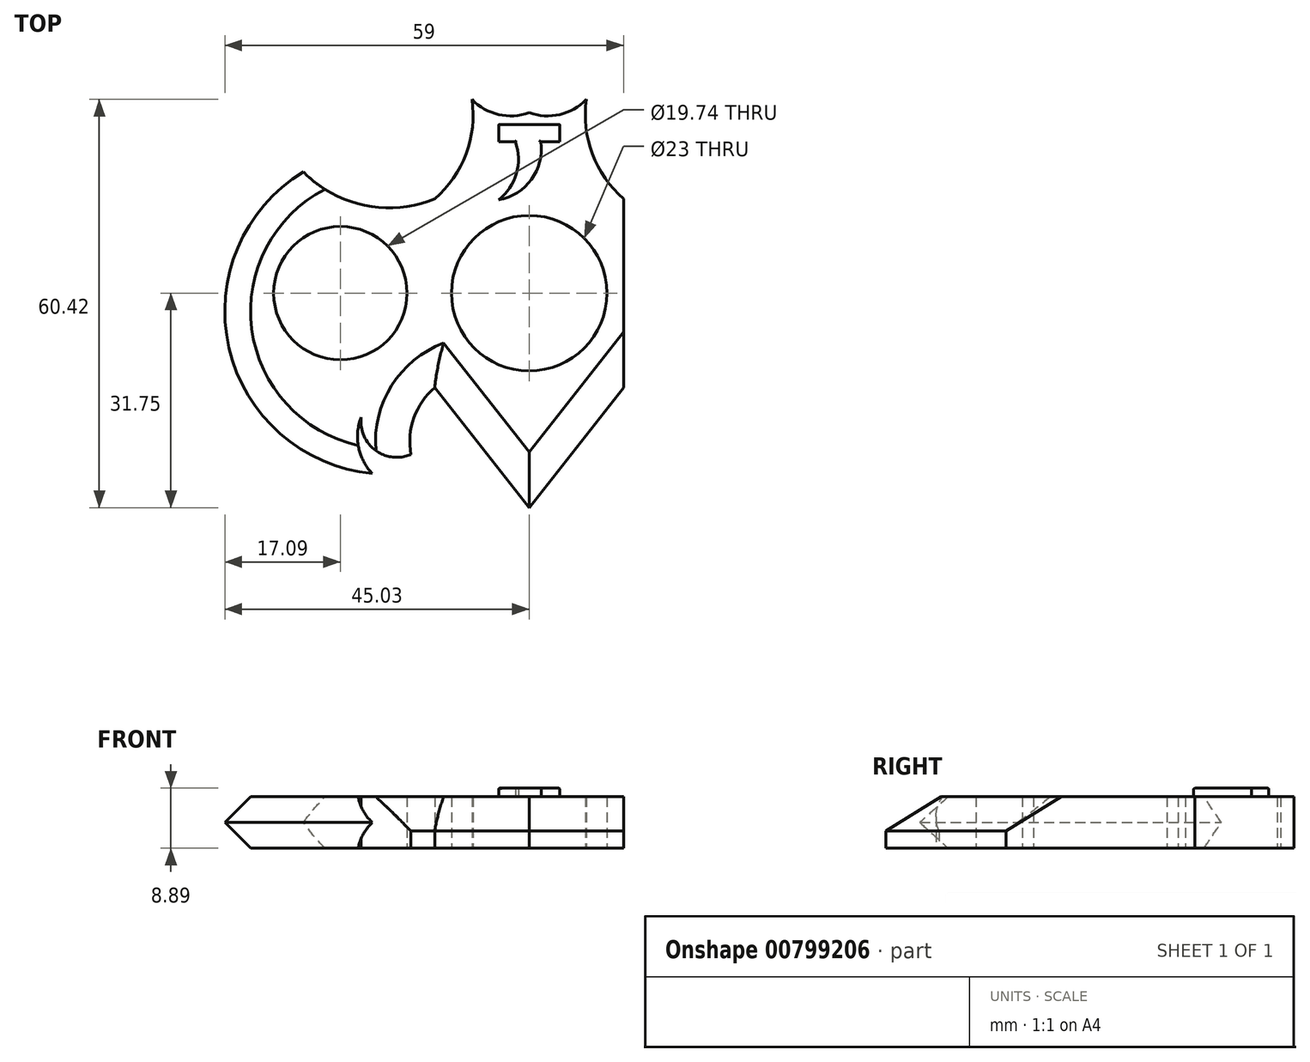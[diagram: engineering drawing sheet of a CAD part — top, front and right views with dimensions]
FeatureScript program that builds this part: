
annotation { "Feature Type Name" : "Feature", "Feature Type Description" : "" }
export const myFeature = defineFeature(function(context is Context, id is Id, definition is map)
    precondition{}
    {
        {
            var Q0;
            Q0=qCreatedBy(makeId("Top.planeOp"),FACE);
            var sketch = newSketch(context, id + "F0", { "sketchPlane" : qUnion([Q0])});
            skCircle(sketch, "E0", {"center": v(0, 0) * mm, "radius": 11.5 * mm});
            skLineSegment(sketch, "E1.bottom", {"start": v(13.97, -13.97) * mm, "end": v(-13.97, -13.97) * mm});
            skLineSegment(sketch, "E1.top", {"start": v(13.97, 13.97) * mm, "end": v(-13.97, 13.97) * mm});
            skLineSegment(sketch, "E1.left", {"start": v(13.97, -13.97) * mm, "end": v(13.97, 13.97) * mm});
            skLineSegment(sketch, "E1.right", {"start": v(-13.97, -13.97) * mm, "end": v(-13.97, 13.97) * mm});
            skArc(sketch, "E2", {"start": v(-34.3, 18.9) * mm, "mid": v(-24.93, 13.13) * mm, "end": v(-13.97, 13.97) * mm});
            skArc(sketch, "E3", {"start": v(-34.3, 18.9) * mm, "mid": v(-45.4, -9.38) * mm, "end": v(-21.46, -28.08) * mm});
            skLineSegment(sketch, "E4", {"start": v(-13.97, -13.97) * mm, "end": v(0, -31.75) * mm});
            skArc(sketch, "E5", {"start": v(-13.97, 13.97) * mm, "mid": v(-9.35, 20.62) * mm, "end": v(-8.45, 28.67) * mm});
            skArc(sketch, "E6", {"start": v(-8.45, 28.67) * mm, "mid": v(-4.52, 26.42) * mm, "end": v(0, 26.71) * mm});
            skLineSegment(sketch, "E7.MirrorCS", {"start": v(13.97, -13.97) * mm, "end": v(0, -31.75) * mm});
            skArc(sketch, "E8.MirrorCS", {"start": v(34.3, 18.9) * mm, "mid": v(24.93, 13.13) * mm, "end": v(13.97, 13.97) * mm});
            skArc(sketch, "E9.MirrorCS", {"start": v(34.3, 18.9) * mm, "mid": v(45.4, -9.38) * mm, "end": v(21.46, -28.08) * mm});
            skArc(sketch, "E10.MirrorCS", {"start": v(8.45, 28.67) * mm, "mid": v(4.52, 26.42) * mm, "end": v(0, 26.71) * mm});
            skArc(sketch, "E11.MirrorCS", {"start": v(13.97, 13.97) * mm, "mid": v(9.35, 20.62) * mm, "end": v(8.45, 28.67) * mm});
            skArc(sketch, "E12", {"start": v(-24.87, -18.38) * mm, "mid": v(-24.96, -23.86) * mm, "end": v(-21.46, -28.08) * mm});
            skArc(sketch, "E13", {"start": v(-24.87, -18.38) * mm, "mid": v(-22.77, -23.25) * mm, "end": v(-17.5, -23.86) * mm});
            skPoint(sketch, "E13.endSnap0", {"position": v(-24.96, -23.86) * mm});
            skArc(sketch, "E14", {"start": v(-13.97, -13.97) * mm, "mid": v(-17.05, -18.44) * mm, "end": v(-17.5, -23.86) * mm});
            skArc(sketch, "E15.MirrorCS", {"start": v(13.97, -13.97) * mm, "mid": v(17.05, -18.44) * mm, "end": v(17.5, -23.86) * mm});
            skPoint(sketch, "E16.MirrorP", {"position": v(24.96, -23.86) * mm});
            skArc(sketch, "E17.MirrorCS", {"start": v(24.87, -18.38) * mm, "mid": v(22.77, -23.25) * mm, "end": v(17.5, -23.86) * mm});
            skArc(sketch, "E18.MirrorCS", {"start": v(24.87, -18.38) * mm, "mid": v(24.96, -23.86) * mm, "end": v(21.46, -28.08) * mm});
            skCircle(sketch, "E19", {"center": v(-27.94, 0) * mm, "radius": 9.87 * mm});
            skCircle(sketch, "E20", {"center": v(27.94, 0) * mm, "radius": 9.87 * mm});
            skSolve(sketch);
        }
        {
            var Q0;
            Q0=makeQuery(id+"F0.imprint","IMPRINT",FACE,{"disambiguationData":[TD([[makeQuery(id+"F0.imprint","IMPRINT",EDGE,{"derivedFrom":sQuery(id+"F0.wireOp",EDGE,"E1.right")}),1.0]])]});
            var Q1;
            Q1=makeQuery(id+"F0.imprint","IMPRINT",FACE,{"disambiguationData":[TD([[makeQuery(id+"F0.imprint","IMPRINT",EDGE,{"derivedFrom":sQuery(id+"F0.wireOp",EDGE,"E1.top")}),-1.0]])]});
            var Q2;
            Q2=makeQuery(id+"F0.imprint","IMPRINT",FACE,{"disambiguationData":[TD([[makeQuery(id+"F0.imprint","IMPRINT",EDGE,{"derivedFrom":sQuery(id+"F0.wireOp",EDGE,"E0")}),-1.0]])]});
            var Q3;
            Q3=makeQuery(id+"F0.imprint","IMPRINT",FACE,{"disambiguationData":[TD([[makeQuery(id+"F0.imprint","IMPRINT",EDGE,{"derivedFrom":sQuery(id+"F0.wireOp",EDGE,"E8.MirrorCS")}),1.0]])]});
            var Q4;
            Q4=makeQuery(id+"F0.imprint","IMPRINT",FACE,{"disambiguationData":[TD([[makeQuery(id+"F0.imprint","IMPRINT",EDGE,{"derivedFrom":sQuery(id+"F0.wireOp",EDGE,"E1.bottom")}),1.0]])]});
            extrude(context, id + "F1", {"entities" : qUnion([Q0, Q1, Q2, Q3, Q4]), "depth" : 7.62 * mm, "offsetDistance" : 25.4 * mm});
        }
        {
            var Q0;
            Q0=makeQuery(id+"F1.opExtrude","CAP_EDGE",EDGE,{"disambiguationData":[OSD([sQuery(id+"F0.wireOp",EDGE,"E4")])],"isStart":false});
            var Q1;
            Q1=makeQuery(id+"F1.opExtrude","CAP_EDGE",EDGE,{"disambiguationData":[OSD([sQuery(id+"F0.wireOp",EDGE,"E7.MirrorCS")])],"isStart":false});
            var Q2;
            Q2=makeQuery(id+"F1.opExtrude","CAP_EDGE",EDGE,{"disambiguationData":[OSD([sQuery(id+"F0.wireOp",EDGE,"E14")])],"isStart":false});
            var Q3;
            Q3=makeQuery(id+"F1.opExtrude","CAP_EDGE",EDGE,{"disambiguationData":[OSD([sQuery(id+"F0.wireOp",EDGE,"E15.MirrorCS")])],"isStart":false});
            var Q4;
            Q4=makeQuery(id+"F1.opExtrude","CAP_EDGE",EDGE,{"disambiguationData":[OSD([sQuery(id+"F0.wireOp",EDGE,"E9.MirrorCS")])],"isStart":false});
            var Q5;
            Q5=makeQuery(id+"F1.opExtrude","CAP_EDGE",EDGE,{"disambiguationData":[OSD([sQuery(id+"F0.wireOp",EDGE,"E3")])],"isStart":false});
            var Q6;
            Q6=makeQuery(id+"F1.opExtrude","CAP_EDGE",EDGE,{"disambiguationData":[OSD([sQuery(id+"F0.wireOp",EDGE,"E3")])],"isStart":true});
            var Q7;
            Q7=makeQuery(id+"F1.opExtrude","CAP_EDGE",EDGE,{"disambiguationData":[OSD([sQuery(id+"F0.wireOp",EDGE,"E9.MirrorCS")])],"isStart":true});
            chamfer(context, id + "F2", {"entities" : qUnion([Q0, Q1, Q2, Q3, Q4, Q5, Q6, Q7]), "width" : 5.08 * mm, "tangentPropagation" : true});
        }
        {
            var Q0;
            Q0=makeQuery(id+"F1.opExtrude","CAP_FACE",FACE,{"disambiguationData":[OSD([sQuery(id+"F0.wireOp",EDGE,"E0"),sQuery(id+"F0.wireOp",EDGE,"E2"),sQuery(id+"F0.wireOp",EDGE,"E3"),sQuery(id+"F0.wireOp",EDGE,"E4"),sQuery(id+"F0.wireOp",EDGE,"E5"),sQuery(id+"F0.wireOp",EDGE,"E6"),sQuery(id+"F0.wireOp",EDGE,"E7.MirrorCS"),sQuery(id+"F0.wireOp",EDGE,"E8.MirrorCS"),sQuery(id+"F0.wireOp",EDGE,"E9.MirrorCS"),sQuery(id+"F0.wireOp",EDGE,"E10.MirrorCS"),sQuery(id+"F0.wireOp",EDGE,"E11.MirrorCS"),sQuery(id+"F0.wireOp",EDGE,"E12"),sQuery(id+"F0.wireOp",EDGE,"E13"),sQuery(id+"F0.wireOp",EDGE,"E14"),sQuery(id+"F0.wireOp",EDGE,"E15.MirrorCS"),sQuery(id+"F0.wireOp",EDGE,"E17.MirrorCS"),sQuery(id+"F0.wireOp",EDGE,"E18.MirrorCS"),sQuery(id+"F0.wireOp",EDGE,"E19"),sQuery(id+"F0.wireOp",EDGE,"E20")])],"isStart":false});
            var sketch = newSketch(context, id + "F3", { "sketchPlane" : qUnion([Q0])});
            skLineSegment(sketch, "E21", {"start": v(-4.52, 24.93) * mm, "end": v(4.52, 24.93) * mm});
            skPoint(sketch, "E21.startSnap0", {"position": v(-4.52, 26.42) * mm});
            skPoint(sketch, "E21.endSnap0", {"position": v(4.52, 26.42) * mm});
            skLineSegment(sketch, "E22", {"start": v(4.52, 24.93) * mm, "end": v(4.52, 22.4) * mm});
            skLineSegment(sketch, "E23", {"start": v(4.52, 22.4) * mm, "end": v(1.7, 22.4) * mm});
            skLineSegment(sketch, "E24", {"start": v(-4.52, 24.93) * mm, "end": v(-4.52, 22.4) * mm});
            skLineSegment(sketch, "E25", {"start": v(-4.52, 22.4) * mm, "end": v(-2.05, 22.4) * mm});
            skArc(sketch, "E26", {"start": v(-4.52, 13.8) * mm, "mid": v(-1.9, 17.7) * mm, "end": v(-2.05, 22.4) * mm});
            skArc(sketch, "E27", {"start": v(-4.52, 13.8) * mm, "mid": v(0.33, 16.84) * mm, "end": v(1.7, 22.4) * mm});
            skSolve(sketch);
        }
        {
            var Q0;
            Q0 = qSketchRegion(id + "F3", true);
            extrude(context, id + "F4", {"entities" : qUnion([Q0]), "operationType" : NewBodyOperationType.ADD, "depth" : 1.27 * mm, "offsetDistance" : 25.4 * mm});
        }
        {
            var Q0;
            Q0=makeQuery(id+"F4.opExtrude","CAP_FACE",FACE,{"disambiguationData":[OSD([sQuery(id+"F3.wireOp",EDGE,"E21"),sQuery(id+"F3.wireOp",EDGE,"E22"),sQuery(id+"F3.wireOp",EDGE,"E23"),sQuery(id+"F3.wireOp",EDGE,"E24"),sQuery(id+"F3.wireOp",EDGE,"E25"),sQuery(id+"F3.wireOp",EDGE,"E26"),sQuery(id+"F3.wireOp",EDGE,"E27")])],"isStart":false});
            fillet(context, id + "F5", {"entities" : qUnion([Q0]), "radius" : 0.18 * mm, "tangentPropagation" : true, "allowEdgeOverflow" : false});
        }
    });
